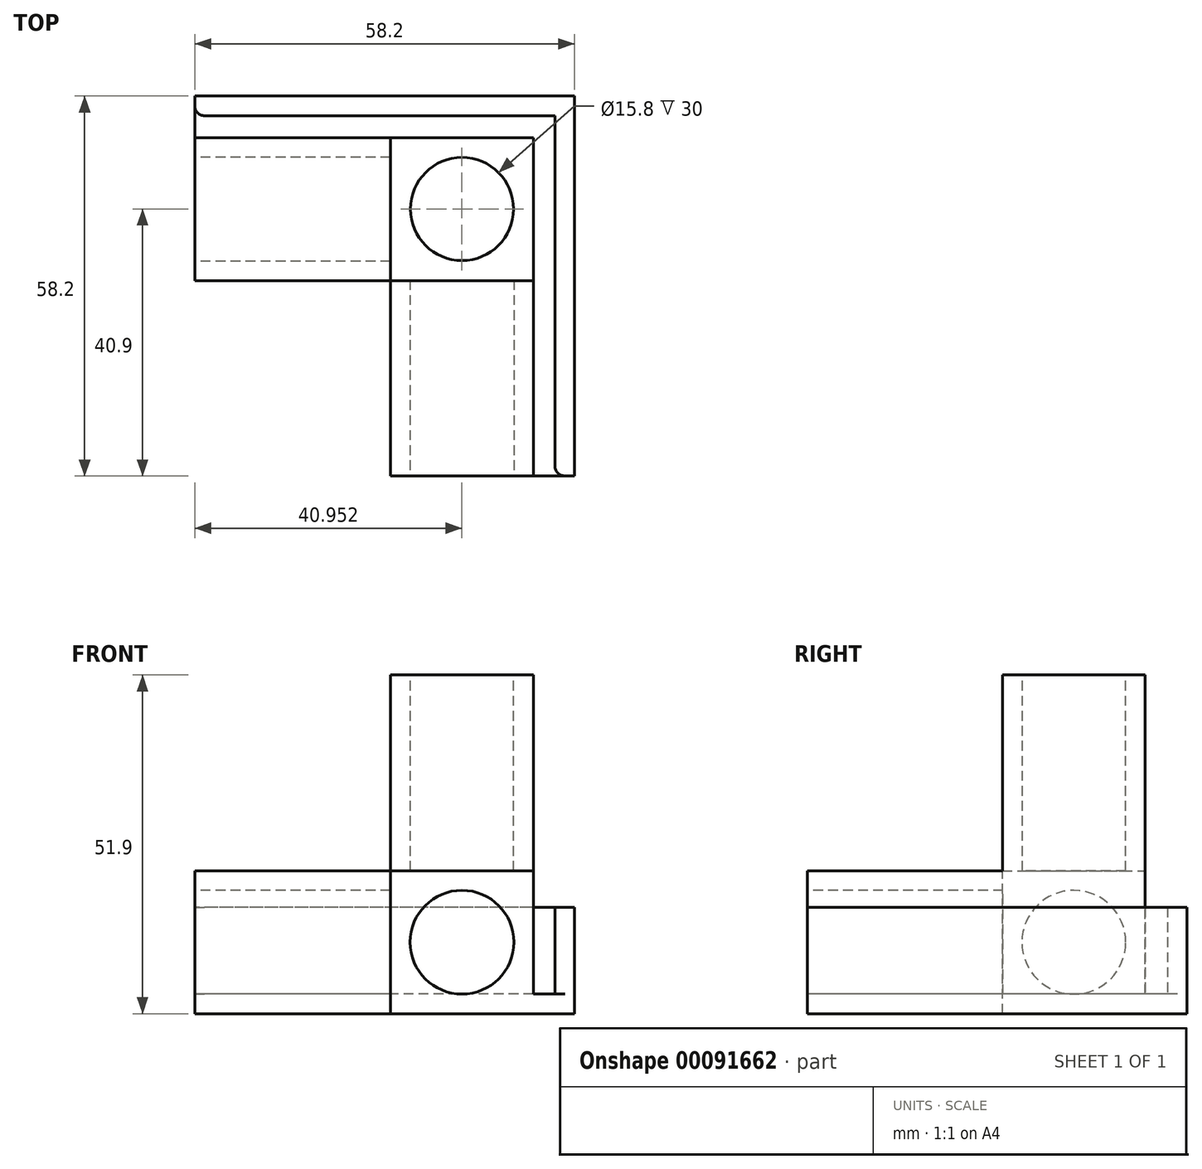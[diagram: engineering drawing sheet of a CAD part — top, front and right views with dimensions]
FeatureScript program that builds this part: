
annotation { "Feature Type Name" : "Feature", "Feature Type Description" : "" }
export const myFeature = defineFeature(function(context is Context, id is Id, definition is map)
    precondition{}
    {
        {
            var Q0;
            Q0=qCreatedBy(makeId("Front.planeOp"),FACE);
            var sketch = newSketch(context, id + "F0", { "sketchPlane" : qUnion([Q0])});
            skLineSegment(sketch, "E0.bottom", {"start": v(-42.3, 45.9) * mm, "end": v(-26.4, 45.9) * mm});
            skLineSegment(sketch, "E0.top", {"start": v(-42.3, 0) * mm, "end": v(-26.4, 0) * mm});
            skLineSegment(sketch, "E0.left", {"start": v(-42.3, 45.9) * mm, "end": v(-42.3, 0) * mm});
            skLineSegment(sketch, "E0.right", {"start": v(-26.4, 45.9) * mm, "end": v(-26.4, 15.9) * mm});
            skLineSegment(sketch, "E1.top", {"start": v(-42.3, 15.9) * mm, "end": v(-26.4, 15.9) * mm});
            skLineSegment(sketch, "E1.left", {"start": v(-42.3, 0) * mm, "end": v(-42.3, 15.9) * mm});
            skLineSegment(sketch, "E1.right", {"start": v(3.6, 0) * mm, "end": v(3.6, 15.9) * mm});
            skLineSegment(sketch, "E2", {"start": v(-26.4, 15.9) * mm, "end": v(-26.4, 0) * mm});
            skLineSegment(sketch, "E3", {"start": v(-26.4, 15.9) * mm, "end": v(3.6, 15.9) * mm});
            skLineSegment(sketch, "E4", {"start": v(-26.4, 0) * mm, "end": v(-26.4, 0) * mm});
            skLineSegment(sketch, "E5", {"start": v(-42.3, 15.9) * mm, "end": v(-42.3, 15.9) * mm});
            skLineSegment(sketch, "E6", {"start": v(-26.4, 0) * mm, "end": v(3.6, 0) * mm});
            skLineSegment(sketch, "E7.0", {"start": v(-45.3, 48.9) * mm, "end": v(-45.3, -3) * mm});
            skLineSegment(sketch, "E7.1", {"start": v(-45.3, -3) * mm, "end": v(-23.4, -3) * mm});
            skLineSegment(sketch, "E7.2", {"start": v(-23.4, 48.9) * mm, "end": v(-23.4, 18.9) * mm});
            skLineSegment(sketch, "E7.3", {"start": v(-23.4, 18.9) * mm, "end": v(6.6, 18.9) * mm});
            skLineSegment(sketch, "E7.4", {"start": v(6.6, -3) * mm, "end": v(6.6, 18.9) * mm});
            skLineSegment(sketch, "E7.5", {"start": v(-45.3, 48.9) * mm, "end": v(-23.4, 48.9) * mm});
            skLineSegment(sketch, "E7.6", {"start": v(-23.4, -3) * mm, "end": v(6.6, -3) * mm});
            skPoint(sketch, "E8", {"position": v(-34.36, 7.95) * mm});
            skPoint(sketch, "E8.positionSnap0", {"position": v(-26.4, 7.95) * mm});
            skPoint(sketch, "E8.positionSnap1", {"position": v(-34.36, 15.9) * mm});
            skCircle(sketch, "E9", {"center": v(-34.36, 7.95) * mm, "radius": 7.95 * mm});
            skLineSegment(sketch, "E10", {"start": v(-23.4, 18.9) * mm, "end": v(-45.3, 18.9) * mm});
            skLineSegment(sketch, "E11", {"start": v(-23.4, 18.9) * mm, "end": v(-23.4, -3) * mm});
            skSolve(sketch);
        }
        {
            var Q0;
            {var subQ1=sQuery(id+"F0.wireOp",EDGE,"E1.top");var subQ3=sQuery(id+"F0.wireOp",EDGE,"E9");var subQ4=makeQuery(id+"F0.imprint","INTERSECT",VERTEX,{"derivedFrom":[subQ1,subQ3]});Q0=makeQuery(id+"F0.imprint","IMPRINT",FACE,{"disambiguationData":[TD([[makeQuery(id+"F0.imprint","IMPRINT",EDGE,{"disambiguationData":[TD([[subQ4,-1.0]])],"derivedFrom":subQ3}),-1.0]])]});}
            var Q1;
            {var subQ0=sQuery(id+"F0.wireOp",EDGE,"E9");var subQ1=makeQuery(id+"F0.imprint","INTERSECT",VERTEX,{"derivedFrom":[sQuery(id+"F0.wireOp",EDGE,"E1.top"),subQ0]});Q1=makeQuery(id+"F0.imprint","IMPRINT",FACE,{"disambiguationData":[TD([[makeQuery(id+"F0.imprint","IMPRINT",EDGE,{"disambiguationData":[TD([[subQ1,1.0]])],"derivedFrom":subQ0}),1.0]])]});}
            var Q2;
            {var subQ5=sQuery(id+"F0.wireOp",EDGE,"E0.bottom");Q2=makeQuery(id+"F0.imprint","IMPRINT",FACE,{"disambiguationData":[TD([[makeQuery(id+"F0.imprint","IMPRINT",EDGE,{"derivedFrom":subQ5}),1.0]])]});}
            var Q3;
            {var subQ0=sQuery(id+"F0.wireOp",EDGE,"E1.right");Q3=makeQuery(id+"F0.imprint","IMPRINT",FACE,{"disambiguationData":[TD([[makeQuery(id+"F0.imprint","IMPRINT",EDGE,{"derivedFrom":subQ0}),1.0]])]});}
            var Q4;
            {var subQ0=sQuery(id+"F0.wireOp",EDGE,"E0.bottom");Q4=makeQuery(id+"F0.imprint","IMPRINT",FACE,{"disambiguationData":[TD([[makeQuery(id+"F0.imprint","IMPRINT",EDGE,{"derivedFrom":subQ0}),-1.0]])]});}
            var Q5;
            {var subQ0=sQuery(id+"F0.wireOp",EDGE,"E1.left");var subQ1=sQuery(id+"F0.wireOp",EDGE,"E0.top");var subQ2=makeQuery(id+"F0.imprint","INTERSECT",VERTEX,{"derivedFrom":[subQ1,subQ0]});Q5=makeQuery(id+"F0.imprint","IMPRINT",FACE,{"disambiguationData":[TD([[makeQuery(id+"F0.imprint","IMPRINT",EDGE,{"disambiguationData":[TD([[subQ2,-1.0]])],"derivedFrom":subQ1}),1.0]])]});}
            var Q6;
            {var subQ1=sQuery(id+"F0.wireOp",EDGE,"E0.top");var subQ3=sQuery(id+"F0.wireOp",EDGE,"E9");var subQ4=makeQuery(id+"F0.imprint","INTERSECT",VERTEX,{"derivedFrom":[subQ1,subQ3]});Q6=makeQuery(id+"F0.imprint","IMPRINT",FACE,{"disambiguationData":[TD([[makeQuery(id+"F0.imprint","IMPRINT",EDGE,{"disambiguationData":[TD([[subQ4,-1.0]])],"derivedFrom":subQ3}),-1.0]])]});}
            var Q7;
            {var subQ1=sQuery(id+"F0.wireOp",EDGE,"E1.top");var subQ3=sQuery(id+"F0.wireOp",EDGE,"E9");var subQ4=makeQuery(id+"F0.imprint","INTERSECT",VERTEX,{"derivedFrom":[subQ1,subQ3]});Q7=makeQuery(id+"F0.imprint","IMPRINT",FACE,{"disambiguationData":[TD([[makeQuery(id+"F0.imprint","IMPRINT",EDGE,{"disambiguationData":[TD([[subQ4,1.0]])],"derivedFrom":subQ3}),-1.0]])]});}
            var Q8;
            {var subQ5=sQuery(id+"F0.wireOp",EDGE,"E1.right");Q8=makeQuery(id+"F0.imprint","IMPRINT",FACE,{"disambiguationData":[TD([[makeQuery(id+"F0.imprint","IMPRINT",EDGE,{"derivedFrom":subQ5}),-1.0]])]});}
            var Q9;
            {var subQ4=sQuery(id+"F0.wireOp",EDGE,"E0.left");var subQ6=sQuery(id+"F0.wireOp",EDGE,"E10");var subQ8=makeQuery(id+"F0.imprint","INTERSECT",VERTEX,{"derivedFrom":[subQ4,subQ6]});Q9=makeQuery(id+"F0.imprint","IMPRINT",FACE,{"disambiguationData":[TD([[makeQuery(id+"F0.imprint","IMPRINT",EDGE,{"disambiguationData":[TD([[subQ8,1.0]])],"derivedFrom":subQ6}),1.0]])]});}
            var Q10;
            {var subQ3=sQuery(id+"F0.wireOp",EDGE,"E11");var subQ5=sQuery(id+"F0.wireOp",EDGE,"E3");var subQ8=makeQuery(id+"F0.imprint","INTERSECT",VERTEX,{"derivedFrom":[subQ5,subQ3]});Q10=makeQuery(id+"F0.imprint","IMPRINT",FACE,{"disambiguationData":[TD([[makeQuery(id+"F0.imprint","IMPRINT",EDGE,{"disambiguationData":[TD([[subQ8,-1.0]])],"derivedFrom":subQ3}),-1.0]])]});}
            var Q11;
            {var subQ14=sQuery(id+"F0.wireOp",EDGE,"E7.1");Q11=makeQuery(id+"F0.imprint","IMPRINT",FACE,{"disambiguationData":[TD([[makeQuery(id+"F0.imprint","IMPRINT",EDGE,{"derivedFrom":subQ14}),1.0]])]});}
            var Q12;
            {var subQ1=sQuery(id+"F0.wireOp",EDGE,"E0.right");var subQ3=sQuery(id+"F0.wireOp",EDGE,"E10");var subQ4=makeQuery(id+"F0.imprint","INTERSECT",VERTEX,{"derivedFrom":[subQ1,subQ3]});Q12=makeQuery(id+"F0.imprint","IMPRINT",FACE,{"disambiguationData":[TD([[makeQuery(id+"F0.imprint","IMPRINT",EDGE,{"disambiguationData":[TD([[subQ4,-1.0]])],"derivedFrom":subQ1}),1.0]])]});}
            extrude(context, id + "F1", {"entities" : qUnion([Q0, Q1, Q2, Q3, Q4, Q5, Q6, Q7, Q8, Q9, Q10, Q11, Q12]), "depth" : (15.9 + 6) * mm});
        }
        {
            var Q0;
            {var subQ14=sQuery(id+"F0.wireOp",EDGE,"E7.1");Q0=makeQuery(id+"F0.imprint","IMPRINT",FACE,{"disambiguationData":[TD([[makeQuery(id+"F0.imprint","IMPRINT",EDGE,{"derivedFrom":subQ14}),1.0]])]});}
            var Q1;
            {var subQ0=sQuery(id+"F0.wireOp",EDGE,"E9");var subQ1=makeQuery(id+"F0.imprint","INTERSECT",VERTEX,{"derivedFrom":[sQuery(id+"F0.wireOp",EDGE,"E1.top"),subQ0]});Q1=makeQuery(id+"F0.imprint","IMPRINT",FACE,{"disambiguationData":[TD([[makeQuery(id+"F0.imprint","IMPRINT",EDGE,{"disambiguationData":[TD([[subQ1,1.0]])],"derivedFrom":subQ0}),1.0]])]});}
            var Q2;
            {var subQ4=sQuery(id+"F0.wireOp",EDGE,"E0.left");var subQ6=sQuery(id+"F0.wireOp",EDGE,"E10");var subQ8=makeQuery(id+"F0.imprint","INTERSECT",VERTEX,{"derivedFrom":[subQ4,subQ6]});Q2=makeQuery(id+"F0.imprint","IMPRINT",FACE,{"disambiguationData":[TD([[makeQuery(id+"F0.imprint","IMPRINT",EDGE,{"disambiguationData":[TD([[subQ8,1.0]])],"derivedFrom":subQ6}),1.0]])]});}
            var Q3;
            {var subQ3=sQuery(id+"F0.wireOp",EDGE,"E11");var subQ5=sQuery(id+"F0.wireOp",EDGE,"E3");var subQ8=makeQuery(id+"F0.imprint","INTERSECT",VERTEX,{"derivedFrom":[subQ5,subQ3]});Q3=makeQuery(id+"F0.imprint","IMPRINT",FACE,{"disambiguationData":[TD([[makeQuery(id+"F0.imprint","IMPRINT",EDGE,{"disambiguationData":[TD([[subQ8,-1.0]])],"derivedFrom":subQ3}),-1.0]])]});}
            var Q4;
            {var subQ1=sQuery(id+"F0.wireOp",EDGE,"E0.right");var subQ3=sQuery(id+"F0.wireOp",EDGE,"E10");var subQ4=makeQuery(id+"F0.imprint","INTERSECT",VERTEX,{"derivedFrom":[subQ1,subQ3]});Q4=makeQuery(id+"F0.imprint","IMPRINT",FACE,{"disambiguationData":[TD([[makeQuery(id+"F0.imprint","IMPRINT",EDGE,{"disambiguationData":[TD([[subQ4,-1.0]])],"derivedFrom":subQ1}),1.0]])]});}
            var Q5;
            {var subQ1=sQuery(id+"F0.wireOp",EDGE,"E1.top");var subQ3=sQuery(id+"F0.wireOp",EDGE,"E9");var subQ4=makeQuery(id+"F0.imprint","INTERSECT",VERTEX,{"derivedFrom":[subQ1,subQ3]});Q5=makeQuery(id+"F0.imprint","IMPRINT",FACE,{"disambiguationData":[TD([[makeQuery(id+"F0.imprint","IMPRINT",EDGE,{"disambiguationData":[TD([[subQ4,1.0]])],"derivedFrom":subQ3}),-1.0]])]});}
            var Q6;
            {var subQ1=sQuery(id+"F0.wireOp",EDGE,"E1.top");var subQ3=sQuery(id+"F0.wireOp",EDGE,"E9");var subQ4=makeQuery(id+"F0.imprint","INTERSECT",VERTEX,{"derivedFrom":[subQ1,subQ3]});Q6=makeQuery(id+"F0.imprint","IMPRINT",FACE,{"disambiguationData":[TD([[makeQuery(id+"F0.imprint","IMPRINT",EDGE,{"disambiguationData":[TD([[subQ4,-1.0]])],"derivedFrom":subQ3}),-1.0]])]});}
            var Q7;
            {var subQ0=sQuery(id+"F0.wireOp",EDGE,"E1.left");var subQ1=sQuery(id+"F0.wireOp",EDGE,"E0.top");var subQ2=makeQuery(id+"F0.imprint","INTERSECT",VERTEX,{"derivedFrom":[subQ1,subQ0]});Q7=makeQuery(id+"F0.imprint","IMPRINT",FACE,{"disambiguationData":[TD([[makeQuery(id+"F0.imprint","IMPRINT",EDGE,{"disambiguationData":[TD([[subQ2,-1.0]])],"derivedFrom":subQ1}),1.0]])]});}
            var Q8;
            {var subQ1=sQuery(id+"F0.wireOp",EDGE,"E0.top");var subQ3=sQuery(id+"F0.wireOp",EDGE,"E9");var subQ4=makeQuery(id+"F0.imprint","INTERSECT",VERTEX,{"derivedFrom":[subQ1,subQ3]});Q8=makeQuery(id+"F0.imprint","IMPRINT",FACE,{"disambiguationData":[TD([[makeQuery(id+"F0.imprint","IMPRINT",EDGE,{"disambiguationData":[TD([[subQ4,-1.0]])],"derivedFrom":subQ3}),-1.0]])]});}
            extrude(context, id + "F2", {"entities" : qUnion([Q0, Q1, Q2, Q3, Q4, Q5, Q6, Q7, Q8]), "operationType" : NewBodyOperationType.ADD, "depth" : (15.8 + 6 + 30) * mm});
        }
        {
            var Q0;
            Q0=makeQuery(id+"F2.opExtrude","CAP_FACE",FACE,{"disambiguationData":[OSD([sQuery(id+"F0.wireOp",EDGE,"E7.0"),sQuery(id+"F0.wireOp",EDGE,"E7.1"),sQuery(id+"F0.wireOp",EDGE,"E10"),sQuery(id+"F0.wireOp",EDGE,"E11")])],"isStart":false});
            var sketch = newSketch(context, id + "F3", { "sketchPlane" : qUnion([Q0])});
            skCircle(sketch, "E12.0", {"center": v(-34.36, 7.95) * mm, "radius": 7.95 * mm});
            skSolve(sketch);
        }
        {
            var Q0;
            Q0=makeQuery(id+"F1.opExtrude","SWEPT_FACE",FACE,{"disambiguationData":[OSD([sQuery(id+"F0.wireOp",EDGE,"E7.5")])]});
            var sketch = newSketch(context, id + "F4", { "sketchPlane" : qUnion([Q0])});
            skPoint(sketch, "E13", {"position": v(-34.36, -3) * mm});
            skPoint(sketch, "E14", {"position": v(-26.4, -10.9) * mm});
            skPoint(sketch, "E15", {"position": v(-34.36, -10.9) * mm});
            skPoint(sketch, "E16", {"position": v(-62.98, 75) * mm});
            skPoint(sketch, "E17.orphan", {"position": v(-42.3, -3) * mm});
            skPoint(sketch, "E18.orphan", {"position": v(-26.4, -3) * mm});
            skPoint(sketch, "E19.orphan", {"position": v(-26.4, -18.8) * mm});
            skCircle(sketch, "E20", {"center": v(-34.36, -10.9) * mm, "radius": 7.9 * mm});
            skSolve(sketch);
        }
        {
            var Q0;
            Q0=makeQuery(id+"F1.opExtrude","SWEPT_FACE",FACE,{"disambiguationData":[OSD([sQuery(id+"F0.wireOp",EDGE,"E7.4")])]});
            var sketch = newSketch(context, id + "F5", { "sketchPlane" : qUnion([Q0])});
            skLineSegment(sketch, "E21.0", {"start": v(-18.9, 15.9) * mm, "end": v(-3, 15.9) * mm});
            skLineSegment(sketch, "E21.1", {"start": v(-18.9, 0) * mm, "end": v(-18.9, 15.9) * mm});
            skLineSegment(sketch, "E21.2", {"start": v(-18.9, 0) * mm, "end": v(-3, 0) * mm});
            skLineSegment(sketch, "E21.3", {"start": v(-3, 0) * mm, "end": v(-3, 15.9) * mm});
            skCircle(sketch, "E22", {"center": v(-10.95, 7.95) * mm, "radius": 7.95 * mm});
            skPoint(sketch, "E22.centerSnap0", {"position": v(-10.95, 0) * mm});
            skPoint(sketch, "E22.centerSnap1", {"position": v(-3, 7.95) * mm});
            skSolve(sketch);
        }
        {
            var Q0;
            Q0=makeQuery(id+"F3.imprint","IMPRINT",FACE,{"disambiguationData":[TD([[makeQuery(id+"F3.imprint","IMPRINT",EDGE,{"derivedFrom":sQuery(id+"F3.wireOp",EDGE,"E12.0")}),1.0]])]});
            extrude(context, id + "F6", {"entities" : qUnion([Q0]), "operationType" : NewBodyOperationType.REMOVE, "oppositeDirection" : true, "depth" : 30 * mm});
        }
        {
            var Q0;
            {var subQ0=sQuery(id+"F5.wireOp",EDGE,"E22");var subQ1=makeQuery(id+"F5.imprint","INTERSECT",VERTEX,{"derivedFrom":[sQuery(id+"F5.wireOp",EDGE,"E21.1"),subQ0]});Q0=makeQuery(id+"F5.imprint","IMPRINT",FACE,{"disambiguationData":[TD([[makeQuery(id+"F5.imprint","IMPRINT",EDGE,{"disambiguationData":[TD([[subQ1,1.0]])],"derivedFrom":subQ0}),1.0]])]});}
            extrude(context, id + "F7", {"entities" : qUnion([Q0]), "operationType" : NewBodyOperationType.REMOVE, "oppositeDirection" : true, "depth" : 30 * mm});
        }
        {
            var Q0;
            Q0=makeQuery(id+"F4.imprint","IMPRINT",FACE,{"disambiguationData":[TD([[makeQuery(id+"F4.imprint","IMPRINT",EDGE,{"derivedFrom":sQuery(id+"F4.wireOp",EDGE,"E20")}),1.0]])]});
            var Q1;
            Q1=sQuery(id+"F4.wireOp",EDGE,"E20");
            extrude(context, id + "F8", {"entities" : qUnion([Q0]), "operationType" : NewBodyOperationType.REMOVE, "surfaceEntities" : qUnion([Q1]), "oppositeDirection" : true, "depth" : 30 * mm});
        }
        {
            var Q0;
            Q0=makeQuery(id+"F2.opExtrude","CAP_FACE",FACE,{"disambiguationData":[OSD([sQuery(id+"F0.wireOp",EDGE,"E7.0"),sQuery(id+"F0.wireOp",EDGE,"E7.1"),sQuery(id+"F0.wireOp",EDGE,"E10"),sQuery(id+"F0.wireOp",EDGE,"E11")])],"isStart":false});
            var sketch = newSketch(context, id + "F9", { "sketchPlane" : qUnion([Q0])});
            skLineSegment(sketch, "E23", {"start": v(-45.3, -3) * mm, "end": v(-51.6, -3) * mm});
            skLineSegment(sketch, "E24", {"start": v(-51.6, -3) * mm, "end": v(-51.6, 13.3) * mm});
            skLineSegment(sketch, "E25", {"start": v(-51.6, 13.3) * mm, "end": v(-48.6, 13.3) * mm});
            skLineSegment(sketch, "E26", {"start": v(-48.6, 13.3) * mm, "end": v(-48.6, 0) * mm});
            skLineSegment(sketch, "E27", {"start": v(-48.6, 0) * mm, "end": v(-45.3, 0) * mm});
            skSolve(sketch);
        }
        {
            var Q0;
            {var subQ0=sQuery(id+"F9.wireOp",EDGE,"E23");Q0=makeQuery(id+"F9.imprint","IMPRINT",FACE,{"disambiguationData":[TD([[makeQuery(id+"F9.imprint","IMPRINT",EDGE,{"derivedFrom":subQ0}),-1.0]])]});}
            extrude(context, id + "F10", {"entities" : qUnion([Q0]), "operationType" : NewBodyOperationType.ADD, "oppositeDirection" : true, "depth" : (6 + 15.9 + 30 + 6.3) * mm});
        }
        {
            var Q0;
            Q0=makeQuery(id+"F1.opExtrude","SWEPT_FACE",FACE,{"disambiguationData":[OSD([sQuery(id+"F0.wireOp",EDGE,"E7.4")])]});
            var sketch = newSketch(context, id + "F11", { "sketchPlane" : qUnion([Q0])});
            skLineSegment(sketch, "E28.0.0", {"start": v(6.4, 0) * mm, "end": v(0, 0) * mm});
            skLineSegment(sketch, "E28.0.1", {"start": v(0, 0) * mm, "end": v(0, -3) * mm});
            skLineSegment(sketch, "E28.0.2", {"start": v(0, -3) * mm, "end": v(6.4, -3) * mm});
            skLineSegment(sketch, "E28.0.3", {"start": v(6.4, -3) * mm, "end": v(6.4, 0) * mm});
            skLineSegment(sketch, "E29.0", {"start": v(6.4, 13.3) * mm, "end": v(6.4, 0) * mm});
            skLineSegment(sketch, "E30", {"start": v(6.4, 13.3) * mm, "end": v(3.4, 13.3) * mm});
            skLineSegment(sketch, "E31", {"start": v(3.4, 13.3) * mm, "end": v(3.4, 0) * mm});
            skSolve(sketch);
        }
        {
            var Q0;
            Q0=qSketchRegion(id+"F11",true);
            extrude(context, id + "F12", {"entities" : qUnion([Q0]), "operationType" : NewBodyOperationType.ADD, "endBound" : BoundingType.UP_TO_NEXT, "oppositeDirection" : true, "depth" : 25 * mm});
        }
        {
            var Q0;
            Q0=makeQuery(id+"F12.opExtrude","CAP_EDGE",EDGE,{"disambiguationData":[OSD([sQuery(id+"F11.wireOp",EDGE,"E31")])],"isStart":true});
            var Q1;
            Q1=makeQuery(id+"F10.opExtrude","CAP_EDGE",EDGE,{"disambiguationData":[OSD([sQuery(id+"F9.wireOp",EDGE,"E26")])],"isStart":true});
            fillet(context, id + "F13", {"entities" : qUnion([Q0, Q1]), "radius" : 1.5 * mm, "tangentPropagation" : true, "allowEdgeOverflow" : false});
        }
        {
            var Q0;
            Q0=makeQuery(id+"F1.opExtrude","SWEPT_BODY",BODY,{"disambiguationData":[OSD([sQuery(id+"F0.wireOp",EDGE,"E7.0"),sQuery(id+"F0.wireOp",EDGE,"E7.1"),sQuery(id+"F0.wireOp",EDGE,"E7.2"),sQuery(id+"F0.wireOp",EDGE,"E7.3"),sQuery(id+"F0.wireOp",EDGE,"E7.4"),sQuery(id+"F0.wireOp",EDGE,"E7.5"),sQuery(id+"F0.wireOp",EDGE,"E7.6")])]});
            var Q1;
            Q1=makeQuery(id+"F12.boolean.opBoolean","MERGE",FACE,{"derivedFrom":[makeQuery(id+"F1.opExtrude","SWEPT_FACE",FACE,{"disambiguationData":[OSD([sQuery(id+"F0.wireOp",EDGE,"E7.4")])]}),makeQuery(id+"F12.opExtrude","CAP_FACE",FACE,{"disambiguationData":[OSD([sQuery(id+"F11.wireOp",EDGE,"E28.0.0"),sQuery(id+"F11.wireOp",EDGE,"E28.0.1"),sQuery(id+"F11.wireOp",EDGE,"E28.0.2"),sQuery(id+"F11.wireOp",EDGE,"E28.0.3"),sQuery(id+"F11.wireOp",EDGE,"E29.0"),sQuery(id+"F11.wireOp",EDGE,"E30"),sQuery(id+"F11.wireOp",EDGE,"E31")])],"isStart":true})]});
            mirror(context, id + "F14", {"entities" : qUnion([Q0]), "mirrorPlane" : qUnion([Q1])});
        }
        {
            var Q0;
            Q0=makeQuery(id+"F1.opExtrude","SWEPT_BODY",BODY,{"disambiguationData":[OSD([sQuery(id+"F0.wireOp",EDGE,"E7.0"),sQuery(id+"F0.wireOp",EDGE,"E7.1"),sQuery(id+"F0.wireOp",EDGE,"E7.2"),sQuery(id+"F0.wireOp",EDGE,"E7.3"),sQuery(id+"F0.wireOp",EDGE,"E7.4"),sQuery(id+"F0.wireOp",EDGE,"E7.5"),sQuery(id+"F0.wireOp",EDGE,"E7.6")])]});
            deleteBodies(context, id + "F15", {"entities" : qUnion([Q0])});
        }
    });
